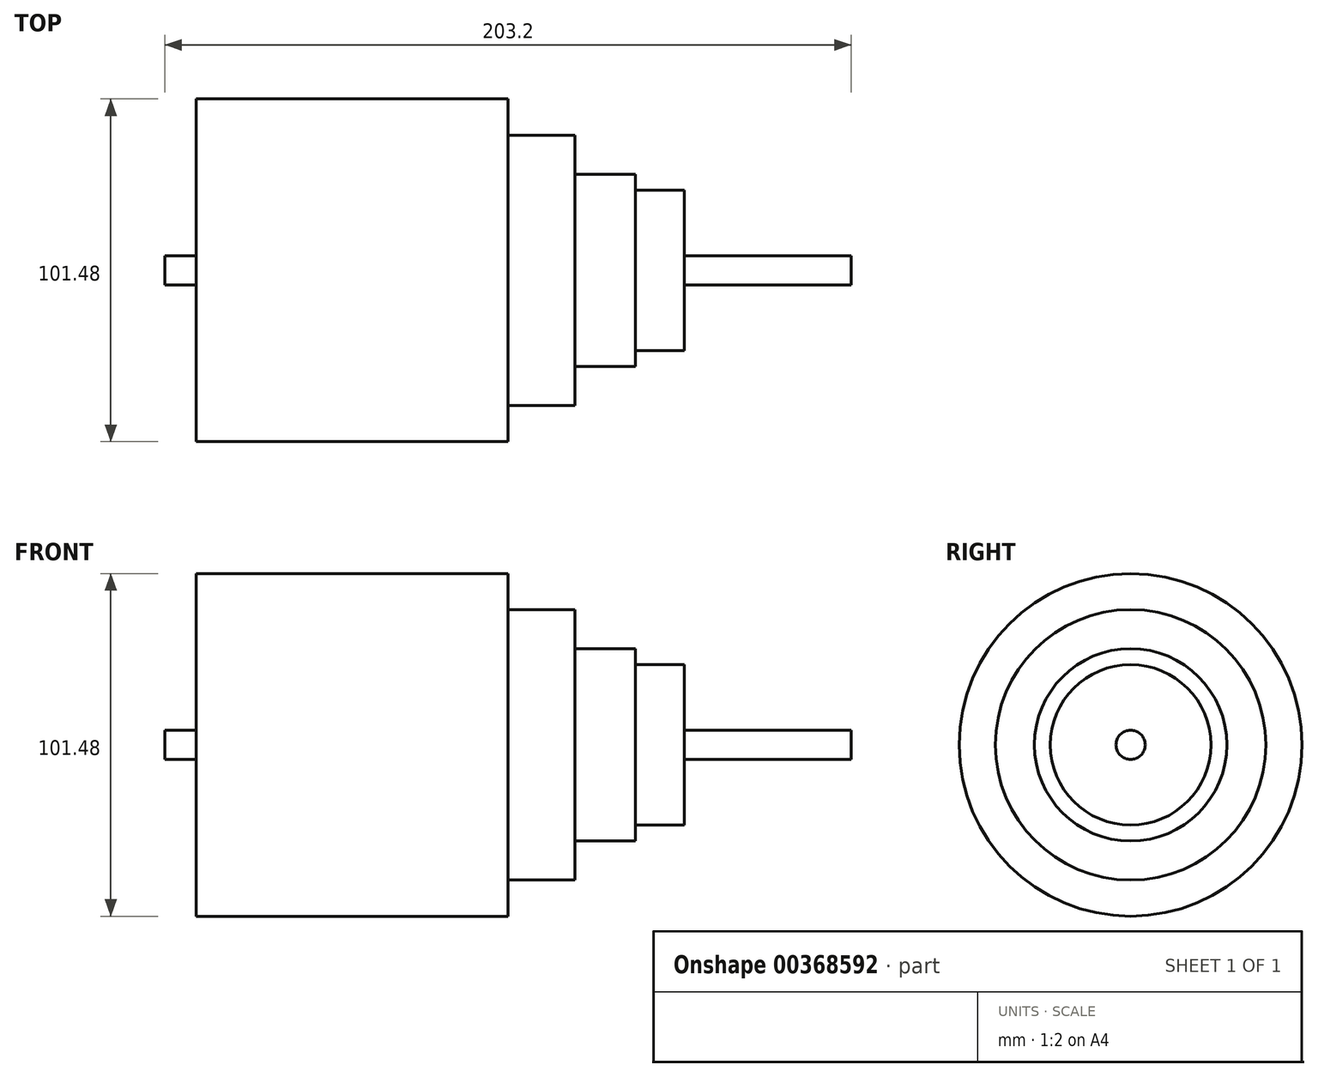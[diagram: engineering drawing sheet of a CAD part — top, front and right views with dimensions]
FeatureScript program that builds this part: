
annotation { "Feature Type Name" : "Feature", "Feature Type Description" : "" }
export const myFeature = defineFeature(function(context is Context, id is Id, definition is map)
    precondition{}
    {
        {
            var Q0;
            Q0=qCreatedBy(makeId("Right.planeOp"),FACE);
            var sketch = newSketch(context, id + "F0", { "sketchPlane" : qUnion([Q0])});
            skCircle(sketch, "E0", {"center": v(0, 0) * mm, "radius": 4.33 * mm});
            skSolve(sketch);
        }
        {
            var Q0;
            Q0 = qSketchRegion(id + "F0", true);
            extrude(context, id + "F1", {"entities" : qUnion([Q0]), "endBound" : BoundingType.SYMMETRIC, "depth" : 203.2 * mm});
        }
        {
            var Q0;
            Q0=qCreatedBy(makeId("Front.planeOp"),FACE);
            var sketch = newSketch(context, id + "F2", { "sketchPlane" : qUnion([Q0])});
            skLineSegment(sketch, "E1.bottom", {"start": v(-92.3, 0) * mm, "end": v(0, 0) * mm});
            skLineSegment(sketch, "E1.top", {"start": v(-92.3, 50.74) * mm, "end": v(0, 50.74) * mm});
            skLineSegment(sketch, "E1.left", {"start": v(-92.3, 0) * mm, "end": v(-92.3, 50.74) * mm});
            skLineSegment(sketch, "E1.right", {"start": v(0, 0) * mm, "end": v(0, 50.74) * mm});
            skLineSegment(sketch, "E2.bottom", {"start": v(0, 0) * mm, "end": v(19.87, 0) * mm});
            skLineSegment(sketch, "E2.top", {"start": v(0, 40.03) * mm, "end": v(19.87, 40.03) * mm});
            skLineSegment(sketch, "E2.left", {"start": v(0, 0) * mm, "end": v(0, 40.03) * mm});
            skLineSegment(sketch, "E2.right", {"start": v(19.87, 0) * mm, "end": v(19.87, 40.03) * mm});
            skLineSegment(sketch, "E3.bottom", {"start": v(19.87, 0) * mm, "end": v(37.78, 0) * mm});
            skLineSegment(sketch, "E3.top", {"start": v(19.87, 28.48) * mm, "end": v(37.78, 28.48) * mm});
            skLineSegment(sketch, "E3.left", {"start": v(19.87, 0) * mm, "end": v(19.87, 28.48) * mm});
            skLineSegment(sketch, "E3.right", {"start": v(37.78, 0) * mm, "end": v(37.78, 28.48) * mm});
            skLineSegment(sketch, "E4.bottom", {"start": v(37.78, 0) * mm, "end": v(52.15, 0) * mm});
            skLineSegment(sketch, "E4.top", {"start": v(37.78, 23.76) * mm, "end": v(52.15, 23.76) * mm});
            skLineSegment(sketch, "E4.left", {"start": v(37.78, 0) * mm, "end": v(37.78, 23.76) * mm});
            skLineSegment(sketch, "E4.right", {"start": v(52.15, 0) * mm, "end": v(52.15, 23.76) * mm});
            skSolve(sketch);
        }
        {
            var Q0;
            Q0=makeQuery(id+"F2.imprint","IMPRINT",FACE,{"disambiguationData":[TD([[makeQuery(id+"F2.imprint","IMPRINT",EDGE,{"derivedFrom":sQuery(id+"F2.wireOp",EDGE,"E1.bottom")}),1.0]])]});
            var Q1;
            Q1=makeQuery(id+"F2.imprint","IMPRINT",FACE,{"disambiguationData":[TD([[makeQuery(id+"F2.imprint","IMPRINT",EDGE,{"derivedFrom":sQuery(id+"F2.wireOp",EDGE,"E2.bottom")}),1.0]])]});
            var Q2;
            Q2=makeQuery(id+"F2.imprint","IMPRINT",FACE,{"disambiguationData":[TD([[makeQuery(id+"F2.imprint","IMPRINT",EDGE,{"derivedFrom":sQuery(id+"F2.wireOp",EDGE,"E3.bottom")}),1.0]])]});
            var Q3;
            Q3=makeQuery(id+"F2.imprint","IMPRINT",FACE,{"disambiguationData":[TD([[makeQuery(id+"F2.imprint","IMPRINT",EDGE,{"derivedFrom":sQuery(id+"F2.wireOp",EDGE,"E4.bottom")}),1.0]])]});
            var Q4;
            Q4=makeQuery(id+"F1.opExtrude","SWEPT_FACE",FACE,{"disambiguationData":[OSD([sQuery(id+"F0.wireOp",EDGE,"E0")])]});
            revolve(context, id + "F3", {"operationType" : NewBodyOperationType.ADD, "entities" : qUnion([Q0, Q1, Q2, Q3]), "axis" : qUnion([Q4]), "revolveType" : RevolveType.ONE_DIRECTION, "angle" : 360 * degree});
        }
    });
